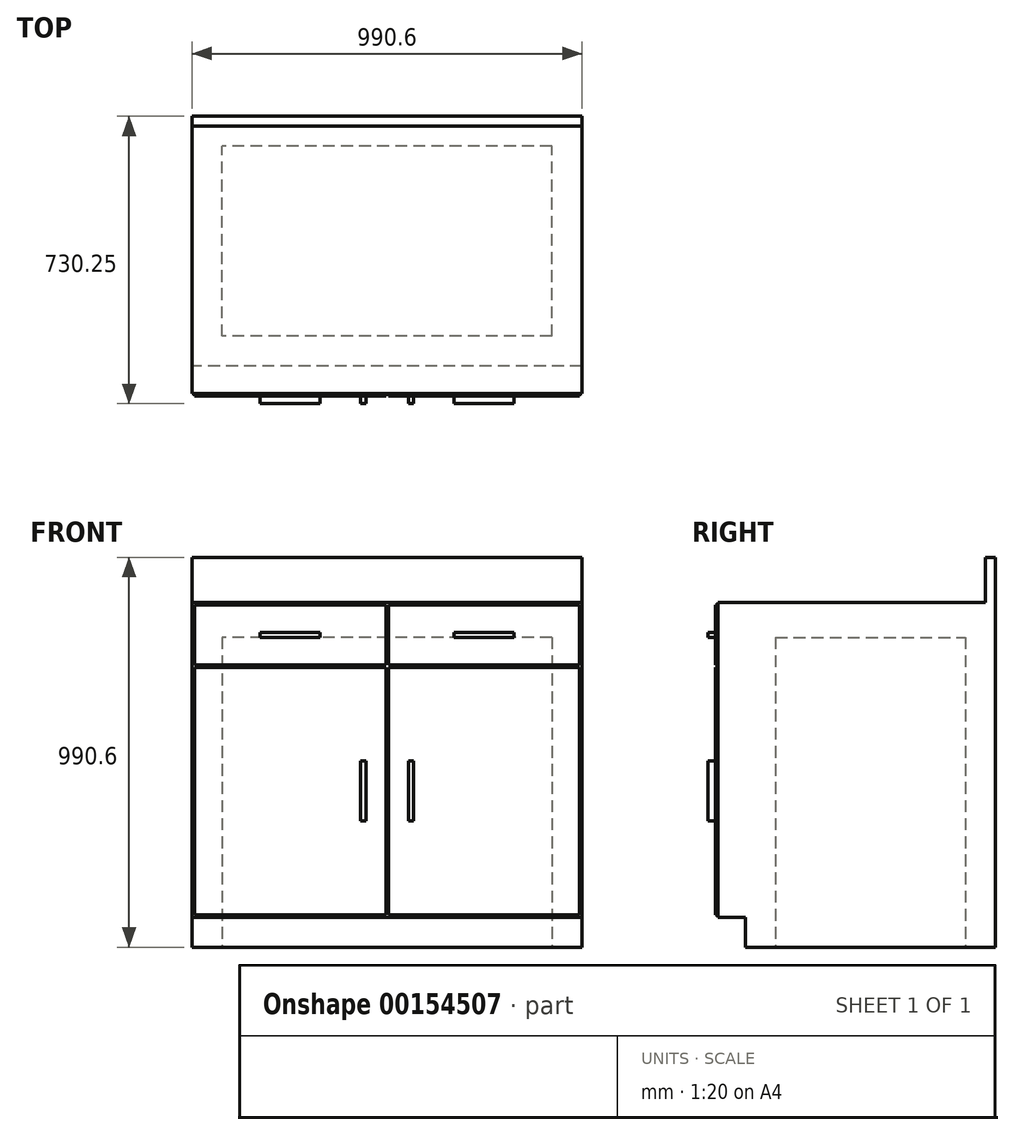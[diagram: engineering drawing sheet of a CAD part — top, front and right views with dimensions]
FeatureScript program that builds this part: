
annotation { "Feature Type Name" : "Feature", "Feature Type Description" : "" }
export const myFeature = defineFeature(function(context is Context, id is Id, definition is map)
    precondition{}
    {
        {
            var Q0;
            Q0=qCreatedBy(makeId("Top.planeOp"),FACE);
            var sketch = newSketch(context, id + "F0", { "sketchPlane" : qUnion([Q0])});
            skLineSegment(sketch, "E0.bottom", {"start": v(495.3, 355.6) * mm, "end": v(-495.3, 355.6) * mm});
            skLineSegment(sketch, "E0.top", {"start": v(495.3, -355.6) * mm, "end": v(-495.3, -355.6) * mm});
            skLineSegment(sketch, "E0.left", {"start": v(495.3, 355.6) * mm, "end": v(495.3, -355.6) * mm});
            skLineSegment(sketch, "E0.right", {"start": v(-495.3, 355.6) * mm, "end": v(-495.3, -355.6) * mm});
            skPoint(sketch, "E0.middle", {"position": v(0, 0) * mm});
            skSolve(sketch);
        }
        {
            var Q0;
            Q0=makeQuery(id+"F0.imprint","IMPRINT",FACE,{"disambiguationData":[TD([[makeQuery(id+"F0.imprint","IMPRINT",EDGE,{"derivedFrom":sQuery(id+"F0.wireOp",EDGE,"E0.bottom")}),1.0]])]});
            extrude(context, id + "F1", {"entities" : qUnion([Q0]), "depth" : 990.6 * mm});
        }
        {
            var Q0;
            Q0=makeQuery(id+"F1.opExtrude","SWEPT_FACE",FACE,{"disambiguationData":[OSD([sQuery(id+"F0.wireOp",EDGE,"E0.top")])]});
            var sketch = newSketch(context, id + "F2", { "sketchPlane" : qUnion([Q0])});
            skLineSegment(sketch, "E1.bottom", {"start": v(-495.3, 990.6) * mm, "end": v(495.3, 990.6) * mm});
            skLineSegment(sketch, "E1.top", {"start": v(-495.3, 876.3) * mm, "end": v(495.3, 876.3) * mm});
            skLineSegment(sketch, "E1.left", {"start": v(-495.3, 990.6) * mm, "end": v(-495.3, 876.3) * mm});
            skLineSegment(sketch, "E1.right", {"start": v(495.3, 990.6) * mm, "end": v(495.3, 876.3) * mm});
            skLineSegment(sketch, "E2.bottom", {"start": v(495.3, 0) * mm, "end": v(-495.3, 0) * mm});
            skLineSegment(sketch, "E2.top", {"start": v(495.3, 76.2) * mm, "end": v(-495.3, 76.2) * mm});
            skLineSegment(sketch, "E2.left", {"start": v(495.3, 0) * mm, "end": v(495.3, 76.2) * mm});
            skLineSegment(sketch, "E2.right", {"start": v(-495.3, 0) * mm, "end": v(-495.3, 76.2) * mm});
            skLineSegment(sketch, "E3.bottom", {"start": v(-488.95, 869.95) * mm, "end": v(-3.18, 869.95) * mm});
            skLineSegment(sketch, "E3.top", {"start": v(-488.95, 717.55) * mm, "end": v(-3.18, 717.55) * mm});
            skLineSegment(sketch, "E3.left", {"start": v(-488.95, 869.95) * mm, "end": v(-488.95, 717.55) * mm});
            skLineSegment(sketch, "E3.right", {"start": v(-3.18, 869.95) * mm, "end": v(-3.18, 717.55) * mm});
            skLineSegment(sketch, "E4.bottom", {"start": v(3.17, 869.95) * mm, "end": v(488.95, 869.95) * mm});
            skLineSegment(sketch, "E4.top", {"start": v(3.17, 717.55) * mm, "end": v(488.95, 717.55) * mm});
            skLineSegment(sketch, "E4.left", {"start": v(3.17, 869.95) * mm, "end": v(3.17, 717.55) * mm});
            skLineSegment(sketch, "E4.right", {"start": v(488.95, 869.95) * mm, "end": v(488.95, 717.55) * mm});
            skLineSegment(sketch, "E5.bottom", {"start": v(488.95, 711.2) * mm, "end": v(3.17, 711.2) * mm});
            skLineSegment(sketch, "E5.top", {"start": v(488.95, 82.55) * mm, "end": v(3.17, 82.55) * mm});
            skLineSegment(sketch, "E5.left", {"start": v(488.95, 711.2) * mm, "end": v(488.95, 82.55) * mm});
            skLineSegment(sketch, "E5.right", {"start": v(3.17, 711.2) * mm, "end": v(3.17, 82.55) * mm});
            skLineSegment(sketch, "E6.bottom", {"start": v(-3.18, 82.55) * mm, "end": v(-488.95, 82.55) * mm});
            skLineSegment(sketch, "E6.top", {"start": v(-3.18, 711.2) * mm, "end": v(-488.95, 711.2) * mm});
            skLineSegment(sketch, "E6.left", {"start": v(-3.18, 82.55) * mm, "end": v(-3.18, 711.2) * mm});
            skLineSegment(sketch, "E6.right", {"start": v(-488.95, 82.55) * mm, "end": v(-488.95, 711.2) * mm});
            skLineSegment(sketch, "E7", {"start": v(-488.95, 793.75) * mm, "end": v(-322.26, 793.75) * mm, "construction": true});
            skLineSegment(sketch, "E8", {"start": v(-322.26, 793.75) * mm, "end": v(-169.86, 793.75) * mm, "construction": true});
            skLineSegment(sketch, "E9", {"start": v(-169.86, 793.75) * mm, "end": v(-3.18, 793.75) * mm, "construction": true});
            skLineSegment(sketch, "E10", {"start": v(495.3, 876.3) * mm, "end": v(495.3, 76.2) * mm});
            skLineSegment(sketch, "E11", {"start": v(-495.3, 876.3) * mm, "end": v(-495.3, 76.2) * mm});
            skLineSegment(sketch, "E12", {"start": v(0, 0) * mm, "end": v(0, 41.15) * mm, "construction": true});
            skLineSegment(sketch, "E13.bottom", {"start": v(-322.26, 800.1) * mm, "end": v(-169.86, 800.1) * mm});
            skLineSegment(sketch, "E13.top", {"start": v(-322.26, 787.4) * mm, "end": v(-169.86, 787.4) * mm});
            skLineSegment(sketch, "E13.left", {"start": v(-322.26, 800.1) * mm, "end": v(-322.26, 787.4) * mm});
            skLineSegment(sketch, "E13.right", {"start": v(-169.86, 800.1) * mm, "end": v(-169.86, 787.4) * mm});
            skLineSegment(sketch, "E14", {"start": v(-488.95, 396.88) * mm, "end": v(-66.68, 396.88) * mm, "construction": true});
            skLineSegment(sketch, "E15.bottom", {"start": v(-66.68, 473.08) * mm, "end": v(-53.98, 473.08) * mm});
            skLineSegment(sketch, "E15.top", {"start": v(-66.68, 320.68) * mm, "end": v(-53.98, 320.68) * mm});
            skLineSegment(sketch, "E15.left", {"start": v(-66.68, 473.08) * mm, "end": v(-66.68, 320.68) * mm});
            skLineSegment(sketch, "E15.right", {"start": v(-53.98, 473.08) * mm, "end": v(-53.98, 320.68) * mm});
            skLineSegment(sketch, "E16.MirrorCS", {"start": v(53.98, 473.08) * mm, "end": v(53.98, 320.68) * mm});
            skLineSegment(sketch, "E17.MirrorCS", {"start": v(66.68, 473.08) * mm, "end": v(66.68, 320.68) * mm});
            skLineSegment(sketch, "E18.MirrorCS", {"start": v(66.68, 473.08) * mm, "end": v(53.98, 473.08) * mm});
            skLineSegment(sketch, "E19.MirrorCS", {"start": v(66.68, 320.68) * mm, "end": v(53.98, 320.68) * mm});
            skLineSegment(sketch, "E20.MirrorCS", {"start": v(322.26, 800.1) * mm, "end": v(169.86, 800.1) * mm});
            skLineSegment(sketch, "E21.MirrorCS", {"start": v(169.86, 800.1) * mm, "end": v(169.86, 787.4) * mm});
            skLineSegment(sketch, "E22.MirrorCS", {"start": v(322.26, 787.4) * mm, "end": v(169.86, 787.4) * mm});
            skLineSegment(sketch, "E23.MirrorCS", {"start": v(322.26, 800.1) * mm, "end": v(322.26, 787.4) * mm});
            skSolve(sketch);
        }
        {
            var Q0;
            Q0=makeQuery(id+"F2.imprint","IMPRINT",FACE,{"disambiguationData":[TD([[makeQuery(id+"F2.imprint","IMPRINT",EDGE,{"derivedFrom":sQuery(id+"F2.wireOp",EDGE,"E1.bottom")}),1.0]])]});
            extrude(context, id + "F3", {"entities" : qUnion([Q0]), "operationType" : NewBodyOperationType.REMOVE, "oppositeDirection" : true, "depth" : 685.8 * mm});
        }
        {
            var Q0;
            Q0=makeQuery(id+"F2.imprint","IMPRINT",FACE,{"disambiguationData":[TD([[makeQuery(id+"F2.imprint","IMPRINT",EDGE,{"derivedFrom":sQuery(id+"F2.wireOp",EDGE,"E1.top")}),-1.0]])]});
            extrude(context, id + "F4", {"entities" : qUnion([Q0]), "operationType" : NewBodyOperationType.REMOVE, "oppositeDirection" : true, "depth" : 6.35 * mm});
        }
        {
            var Q0;
            Q0=makeQuery(id+"F2.imprint","IMPRINT",FACE,{"disambiguationData":[TD([[makeQuery(id+"F2.imprint","IMPRINT",EDGE,{"derivedFrom":sQuery(id+"F2.wireOp",EDGE,"E2.bottom")}),-1.0]])]});
            extrude(context, id + "F5", {"entities" : qUnion([Q0]), "operationType" : NewBodyOperationType.REMOVE, "oppositeDirection" : true, "depth" : 76.2 * mm});
        }
        {
            var Q0;
            Q0=makeQuery(id+"F2.imprint","IMPRINT",FACE,{"disambiguationData":[TD([[makeQuery(id+"F2.imprint","IMPRINT",EDGE,{"derivedFrom":sQuery(id+"F2.wireOp",EDGE,"E13.bottom")}),-1.0]])]});
            var Q1;
            Q1=makeQuery(id+"F2.imprint","IMPRINT",FACE,{"disambiguationData":[TD([[makeQuery(id+"F2.imprint","IMPRINT",EDGE,{"derivedFrom":sQuery(id+"F2.wireOp",EDGE,"E20.MirrorCS")}),1.0]])]});
            var Q2;
            Q2=makeQuery(id+"F2.imprint","IMPRINT",FACE,{"disambiguationData":[TD([[makeQuery(id+"F2.imprint","IMPRINT",EDGE,{"derivedFrom":sQuery(id+"F2.wireOp",EDGE,"E16.MirrorCS")}),1.0]])]});
            var Q3;
            Q3=makeQuery(id+"F2.imprint","IMPRINT",FACE,{"disambiguationData":[TD([[makeQuery(id+"F2.imprint","IMPRINT",EDGE,{"derivedFrom":sQuery(id+"F2.wireOp",EDGE,"E15.bottom")}),-1.0]])]});
            extrude(context, id + "F6", {"entities" : qUnion([Q0, Q1, Q2, Q3]), "operationType" : NewBodyOperationType.ADD, "depth" : 19.05 * mm});
        }
        {
            var Q0;
            Q0=makeQuery(id+"F1.opExtrude","CAP_FACE",FACE,{"disambiguationData":[OSD([sQuery(id+"F0.wireOp",EDGE,"E0.bottom"),sQuery(id+"F0.wireOp",EDGE,"E0.top"),sQuery(id+"F0.wireOp",EDGE,"E0.left"),sQuery(id+"F0.wireOp",EDGE,"E0.right")])],"isStart":true});
            var sketch = newSketch(context, id + "F7", { "sketchPlane" : qUnion([Q0])});
            skLineSegment(sketch, "E24.bottom", {"start": v(419.1, 203.2) * mm, "end": v(-419.1, 203.2) * mm});
            skLineSegment(sketch, "E24.top", {"start": v(419.1, -279.4) * mm, "end": v(-419.1, -279.4) * mm});
            skLineSegment(sketch, "E24.left", {"start": v(419.1, 203.2) * mm, "end": v(419.1, -279.4) * mm});
            skLineSegment(sketch, "E24.right", {"start": v(-419.1, 203.2) * mm, "end": v(-419.1, -279.4) * mm});
            skSolve(sketch);
        }
        {
            var Q0;
            Q0=makeQuery(id+"F7.imprint","IMPRINT",FACE,{"disambiguationData":[TD([[makeQuery(id+"F7.imprint","IMPRINT",EDGE,{"derivedFrom":sQuery(id+"F7.wireOp",EDGE,"E24.bottom")}),1.0]])]});
            extrude(context, id + "F8", {"entities" : qUnion([Q0]), "operationType" : NewBodyOperationType.REMOVE, "oppositeDirection" : true, "depth" : 787.4 * mm});
        }
    });
